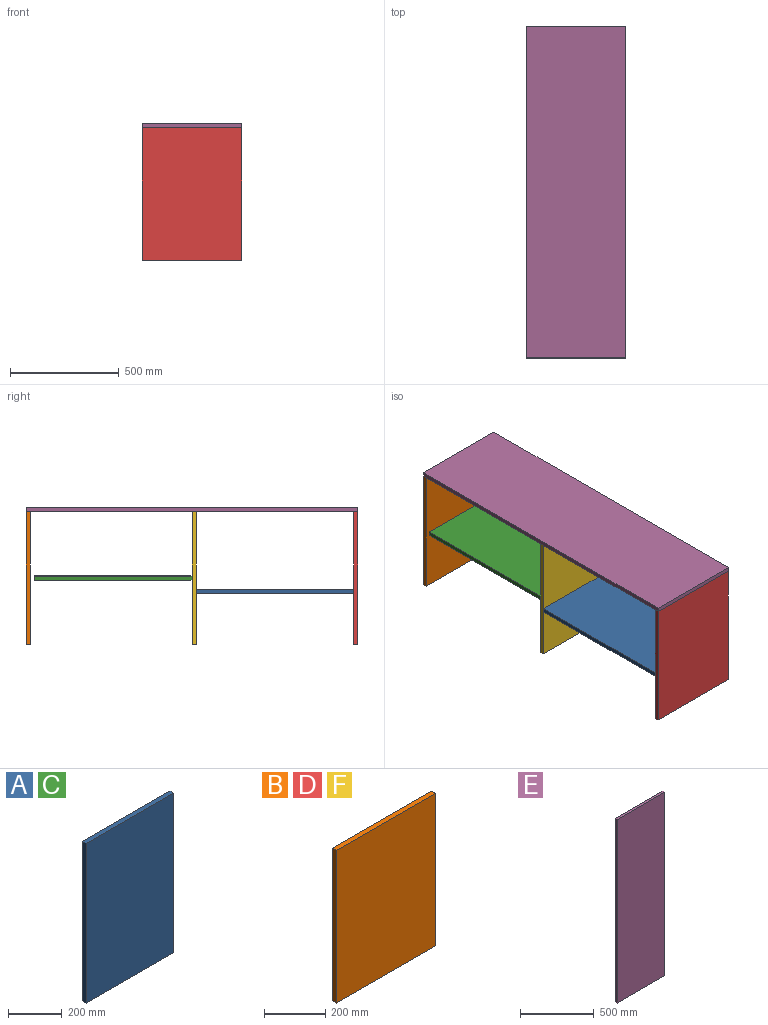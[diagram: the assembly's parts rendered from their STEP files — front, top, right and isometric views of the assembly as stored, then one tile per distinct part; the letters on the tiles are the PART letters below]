
ASSEMBLY  parts=6 mates=14
PART A: 6 faces, bbox 457.2x19.1x723.9 mm
  f0: plane 457.2x19.05mm, normal (0,0,1), area 8709.7mm2, adj f1,f3,f4,f5
  f1: plane 723.9x19.05mm, normal (-1,0,0), area 13790.3mm2, adj f0,f2,f4,f5
  f2: plane 457.2x19.05mm, normal (0,0,-1), area 8709.7mm2, adj f1,f3,f4,f5
  f3: plane 723.9x19.05mm, normal (1,0,0), area 13790.3mm2, adj f0,f2,f4,f5
  f4: plane 723.9x457.2mm, normal (0,-1,0), area 330967.1mm2, adj f0,f1,f2,f3
  f5: plane 723.9x457.2mm, normal (0,1,0), area 330967.1mm2, adj f0,f1,f2,f3
PART B: 6 faces, bbox 457.2x19.1x609.6 mm
  f0: plane 457.2x19.05mm, normal (0,0,1), area 8709.7mm2, adj f1,f3,f4,f5
  f1: plane 609.6x19.05mm, normal (-1,0,0), area 11612.9mm2, adj f0,f2,f4,f5
  f2: plane 457.2x19.05mm, normal (0,0,-1), area 8709.7mm2, adj f1,f3,f4,f5
  f3: plane 609.6x19.05mm, normal (1,0,0), area 11612.9mm2, adj f0,f2,f4,f5
  f4: plane 609.6x457.2mm, normal (0,-1,0), area 278709.1mm2, adj f0,f1,f2,f3
  f5: plane 609.6x457.2mm, normal (0,1,0), area 278709.1mm2, adj f0,f1,f2,f3
PART C: same geometry as A
PART D: same geometry as B
PART E: 6 faces, bbox 457.2x19.1x1524 mm
  f0: plane 457.2x19.05mm, normal (0,0,1), area 8709.7mm2, adj f1,f3,f4,f5
  f1: plane 1524x19.05mm, normal (-1,0,0), area 29032.2mm2, adj f0,f2,f4,f5
  f2: plane 457.2x19.05mm, normal (0,0,-1), area 8709.7mm2, adj f1,f3,f4,f5
  f3: plane 1524x19.05mm, normal (1,0,0), area 29032.2mm2, adj f0,f2,f4,f5
  f4: plane 1524x457.2mm, normal (0,-1,0), area 696772.8mm2, adj f0,f1,f2,f3
  f5: plane 1524x457.2mm, normal (0,1,0), area 696772.8mm2, adj f0,f1,f2,f3
PART F: same geometry as B
PLACE A rot(axis=(1,0,0),90deg) t=(0,742.95,254.53)mm
PLACE B t=(0,1524,0)mm
PLACE C rot(axis=(-1,0,0),90deg) t=(0,762,295.28)mm
PLACE D t=(0,19.05,0)mm
PLACE E rot(axis=(1,0,0),90deg) t=(0,1524,628.65)mm
PLACE F rot(axis=(0,0,-1),180deg) t=(457.2,742.95,0)mm
MATE planar B.f3 <-> E.f3  axis (1,0,0) through (457.2,1514.48,304.8)mm
MATE planar C.f3 <-> F.f1  axis (1,0,0) through (457.2,1123.95,304.8)mm
MATE planar F.f0 <-> E.f4  axis (0,0,1) through (228.6,752.47,609.6)mm
MATE planar E.f3 <-> D.f3  axis (1,0,0) through (457.2,762,619.12)mm
MATE planar E.f4 <-> D.f0  axis (0,0,-1) through (228.6,762,609.6)mm
MATE planar F.f4 <-> C.f2  axis (0,1,0) through (228.6,762,304.8)mm
MATE planar D.f4 <-> E.f0  axis (0,-1,0) through (228.6,0,304.8)mm
MATE planar A.f0 <-> D.f5  axis (0,-1,0) through (228.6,19.05,245.01)mm
MATE planar A.f3 <-> D.f3  axis (1,0,0) through (457.2,381,245.01)mm
MATE planar F.f5 <-> A.f2  axis (0,-1,0) through (228.6,742.95,304.8)mm
MATE planar C.f3 <-> B.f3  axis (1,0,0) through (457.2,1123.95,304.8)mm
MATE planar B.f0 <-> E.f4  axis (0,0,1) through (457.2,1524,609.6)mm
MATE planar F.f1 <-> E.f3  axis (1,0,0) through (457.2,752.47,304.8)mm
MATE planar E.f2 <-> B.f5  axis (0,1,0) through (228.6,1524,619.12)mm
